# Revit family: Dallmeier_PTZ_Indoor_en
name_source: partatom
category: Sicherheitsgeräte
units: mm (PartAtom-declared; Revit-internal decimal feet)

## family parameters
Basisbauteil = Fläche
Beim Laden mit Abzugskörper schneiden = Nein
Bemaßung runder Anschluss = Durchmesser verwenden
Beschriftungsausrichtung beibehalten = Nein
Gemeinsam genutzt = Nein
Raumberechnungspunkt = Nein
Teiletyp = Normal

## types (4) — shared parameters
Hersteller = Dallmeier electronics GmbH
Pixel Horizontal 16:9 = 1920
Pixel Horizontal 4:3 = 1920
URL = https://www.dallmeier.com
Vorgabe-Ansicht = 122 cm
dimensions = Ø245x267mm / Ø179x266mm
number of sensors = 1
operating temperature = -10°C to +50°C
power consumption = 25 W
voltage supply = 24 V
weight = 3,50 kg

## per-type parameters (varying)
| type | Long Horizontal FOV | Modell | Short Horizontal FOV |
| DDZ 4220 HD Indoor | 58,00° | DDZ 4220 HD Indoor | 3,00° |
| DDZ 4230 HD Indoor | 66,00° | DDZ 4230 HD Indoor | 2,00° |
| DDZ 5220 HD Indoor | 58,00° | DDZ 5220 HD-DN/IR | 3,00° |
| DDZ 5232 HD Indoor | 61,40° | DDZ 5232 HD Indoor | 2,10° |

## geometry (parser evidence)
native form markers: Sweep x51
no freeform markers — native parametric forms only
